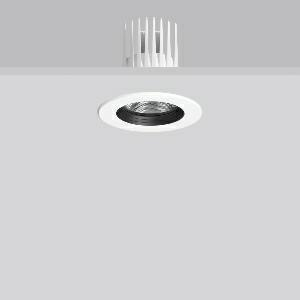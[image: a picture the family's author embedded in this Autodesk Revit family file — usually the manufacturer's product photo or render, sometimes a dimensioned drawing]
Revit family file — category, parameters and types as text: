
# Revit family: heledon_mini_e_901742_002_5a63
name_source: partatom
category: Lighting Fixtures
units: mm (PartAtom-declared; Revit-internal decimal feet)

## family parameters
Cut with Voids When Loaded = No
Host = Face
Light Source = No
Part Type = Normal
Room Calculation Point = No
Round Connector Dimension = Use Diameter
Shared = No

## types (1)
- HELEDON mini E (1 x LED Modul 930, 2550 lm, 3000)
    Apparent Load = 20 VA
    Approval mark = CE
    CIE Flux Codes = 95 99 100 100 100
    Color Rendering = 90
    Color Temperature = 3000
    Default Elevation = 1800 mm
    Description = Series: HELEDON mini
Round recessed downlight. Housing: die-cast aluminium, powder-coated. Black plastic ring and recessed LED to prevent glare from the side. Optical assembly with reflector made of MIRO-Silver with 98% total light reflection for outstanding efficiency - can be changed without tools. Best colour rendering index Ra>90. Suitable for Recessed ceiling mounting. Installation without tools thanks to spring fastening system. Including separate LED converter with connecting cable 600 mm.High quality converter without flickering and stroboscopic effect. Through-wiring box (5 pole) available as accessory. The following accessories can be mounted without use of tools: interchangeable lenses, decorative glasses, honeycomb louvre, clear and frosted diffusers, white interchangeable plastic ring. 
Colour: traffic white, matt (RAL 9016)
Diameter: 124 mm
Height: 3 mm
Cut-out diameter: 114 mm
Recess height: 170 mm
Luminaire: recess height: 120 mm
Lamp: LED
Socket: without socket
Colour temperature: 3000K
Colour rendering index (CRI): 92
System power: 20 W
Rated luminous flux: 2550 lm
Luminous efficiency: 128 lm/W
Control gear: Regulated power supply
Protection class: II
Type of protection: IP 20
    Height = 0 mm  [stored 0 ft]
    Lamp = 1 x LED Modul 930
    Lamp Light Flux = 2550 lm
    Lamp count = 1
    Length = 124 mm  [stored 0.406824 ft]
    Lifetime = 50000 h
    Luminous efficacy = 128 lm/W
    Manufacturer = RZB
    ModVariant = No
    Model = 901742.002
    Mounting Place = Ceiling
    Mounting Type = Recessed
    Number of Poles = 1
    OnlyDefault = Yes
    Power Factor = 1
    Product Name = HELEDON mini E
    Product group = Recessed downlights
    ProductGroupID = 402
    Protection Class = Protection class II
    Protection Degree = IP 20
    RLX_Detail_Level = 1
    RLX_Emergency_Light_Flux = 0 lm
    RLX_Emergency_Type = 0
    RLX_Emergency_Type_DB = No
    RlxData = <blob elided: 125601 chars, md5=43b1ea2e>
    Socket = socket
    Standby Power = 0 W
    System Light Flux = 2550 lm
    System Power = 20 W
    Type Comments = Product without accessories
    Type Image = 901657.002.jpg
    URL = http://relux.com
    VarID = ---
    Voltage = 230 V
    Voltage Range = 220-240 V
    Weight = 0.00 kg
    Width = 0 mm  [stored 0 ft]

note: [stored X ft] marks values corroborated as IEEE doubles in the binary element streams (Revit-internal decimal feet)

## geometry (parser evidence)
native form markers: Blend x4, Sweep x12
no freeform markers — native parametric forms only
